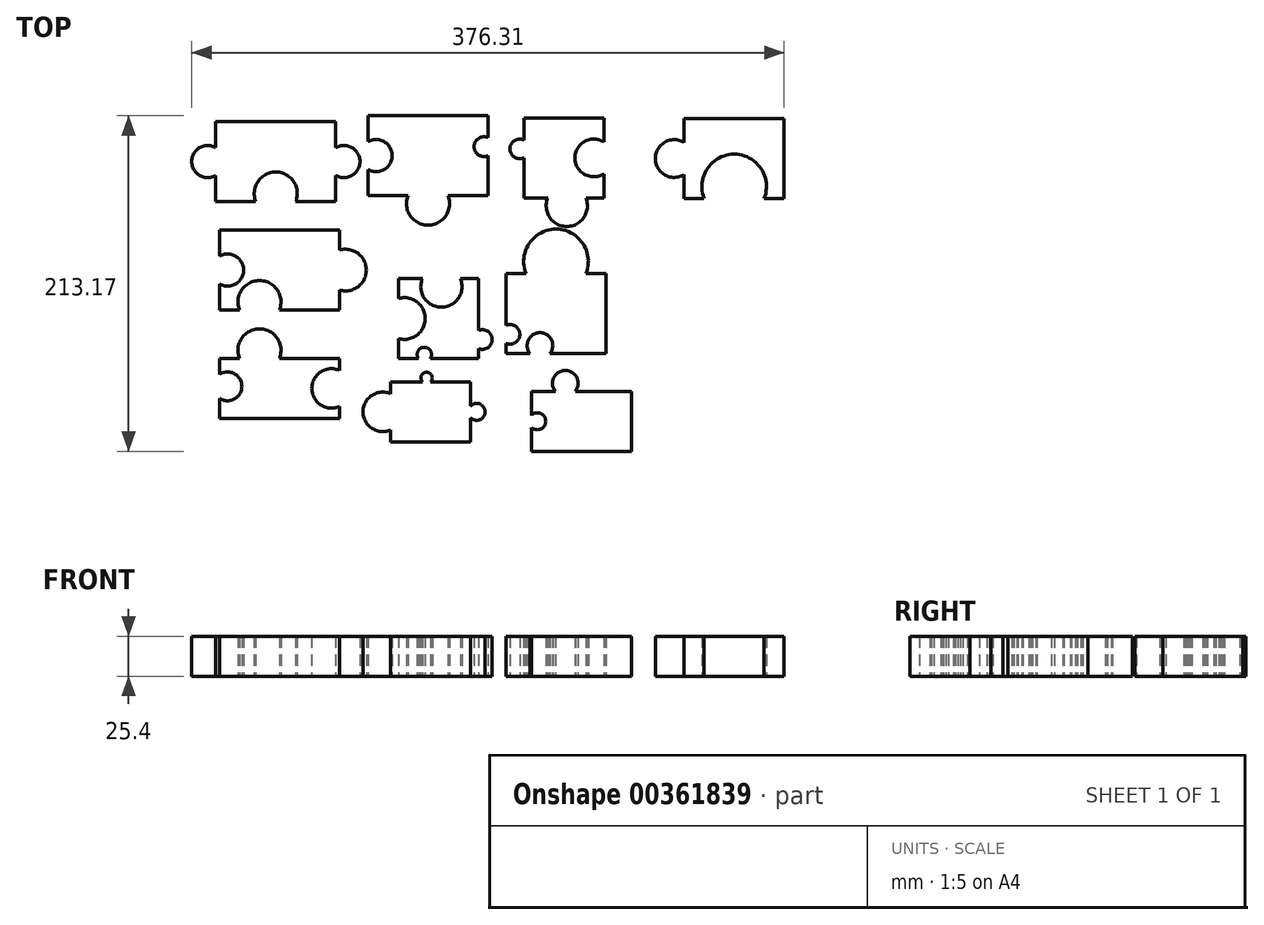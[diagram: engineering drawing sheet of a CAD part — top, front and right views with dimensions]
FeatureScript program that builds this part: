
annotation { "Feature Type Name" : "Feature", "Feature Type Description" : "" }
export const myFeature = defineFeature(function(context is Context, id is Id, definition is map)
    precondition{}
    {
        {
            var Q0;
            Q0=qCreatedBy(makeId("Top.planeOp"),FACE);
            var sketch = newSketch(context, id + "F0", { "sketchPlane" : qUnion([Q0])});
            skLineSegment(sketch, "E0.bottom", {"start": v(-78.54, 63.45) * mm, "end": v(-2.34, 63.45) * mm});
            skLineSegment(sketch, "E0.top", {"start": v(-78.54, 12.65) * mm, "end": v(-2.34, 12.65) * mm});
            skLineSegment(sketch, "E0.left", {"start": v(-78.54, 63.45) * mm, "end": v(-78.54, 12.65) * mm});
            skLineSegment(sketch, "E0.right", {"start": v(-2.34, 63.45) * mm, "end": v(-2.34, 12.65) * mm});
            skArc(sketch, "E1", {"start": v(-27.74, 12.65) * mm, "mid": v(-40.44, 31.4) * mm, "end": v(-53.14, 12.65) * mm});
            skArc(sketch, "E2", {"start": v(-78.54, 46.94) * mm, "mid": v(-93.86, 38.05) * mm, "end": v(-78.54, 29.16) * mm});
            skArc(sketch, "E3", {"start": v(-2.34, 29.16) * mm, "mid": v(12.98, 38.05) * mm, "end": v(-2.34, 46.94) * mm});
            skSolve(sketch);
        }
        {
            var Q0;
            {var subQ0=sQuery(id+"F0.wireOp",EDGE,"E2");Q0=makeQuery(id+"F0.imprint","IMPRINT",FACE,{"disambiguationData":[TD([[makeQuery(id+"F0.imprint","IMPRINT",EDGE,{"derivedFrom":subQ0}),1.0]])]});}
            var Q1;
            {var subQ1=sQuery(id+"F0.wireOp",EDGE,"E0.bottom");Q1=makeQuery(id+"F0.imprint","IMPRINT",FACE,{"disambiguationData":[TD([[makeQuery(id+"F0.imprint","IMPRINT",EDGE,{"derivedFrom":subQ1}),-1.0]])]});}
            var Q2;
            {var subQ0=sQuery(id+"F0.wireOp",EDGE,"E3");Q2=makeQuery(id+"F0.imprint","IMPRINT",FACE,{"disambiguationData":[TD([[makeQuery(id+"F0.imprint","IMPRINT",EDGE,{"derivedFrom":subQ0}),1.0]])]});}
            extrude(context, id + "F1", {"entities" : qUnion([Q0, Q1, Q2]), "depth" : 25.4 * mm});
        }
        {
            var Q0;
            Q0=qCreatedBy(makeId("Top.planeOp"),FACE);
            var sketch = newSketch(context, id + "F2", { "sketchPlane" : qUnion([Q0])});
            skLineSegment(sketch, "E4.bottom", {"start": v(18.15, 67.2) * mm, "end": v(94.35, 67.2) * mm});
            skLineSegment(sketch, "E4.top", {"start": v(18.15, 16.4) * mm, "end": v(94.35, 16.4) * mm});
            skLineSegment(sketch, "E4.left", {"start": v(18.15, 67.2) * mm, "end": v(18.15, 16.4) * mm});
            skLineSegment(sketch, "E4.right", {"start": v(94.35, 67.2) * mm, "end": v(94.35, 16.4) * mm});
            skArc(sketch, "E5", {"start": v(18.15, 32.91) * mm, "mid": v(33.47, 41.8) * mm, "end": v(18.15, 50.7) * mm});
            skArc(sketch, "E6", {"start": v(43.55, 16.4) * mm, "mid": v(56.25, -2.35) * mm, "end": v(68.95, 16.4) * mm});
            skArc(sketch, "E7", {"start": v(94.35, 53.23) * mm, "mid": v(85.55, 47.52) * mm, "end": v(94.35, 41.8) * mm});
            skSolve(sketch);
        }
        {
            var Q0;
            {var subQ0=sQuery(id+"F2.wireOp",EDGE,"E6");Q0=makeQuery(id+"F2.imprint","IMPRINT",FACE,{"disambiguationData":[TD([[makeQuery(id+"F2.imprint","IMPRINT",EDGE,{"derivedFrom":subQ0}),1.0]])]});}
            var Q1;
            {var subQ7=sQuery(id+"F2.wireOp",EDGE,"E4.bottom");Q1=makeQuery(id+"F2.imprint","IMPRINT",FACE,{"disambiguationData":[TD([[makeQuery(id+"F2.imprint","IMPRINT",EDGE,{"derivedFrom":subQ7}),-1.0]])]});}
            var Q2;
            Q2 = qSketchRegion(id + "F8", true);
            extrude(context, id + "F3", {"entities" : qUnion([Q0, Q1, Q2]), "depth" : 25.4 * mm});
        }
        {
            var Q0;
            Q0=qCreatedBy(makeId("Top.planeOp"),FACE);
            var sketch = newSketch(context, id + "F4", { "sketchPlane" : qUnion([Q0])});
            skLineSegment(sketch, "E8.bottom", {"start": v(-76.2, -5.49) * mm, "end": v(0, -5.49) * mm});
            skLineSegment(sketch, "E8.top", {"start": v(-76.2, -56.29) * mm, "end": v(0, -56.29) * mm});
            skLineSegment(sketch, "E8.left", {"start": v(-76.2, -5.49) * mm, "end": v(-76.2, -56.29) * mm});
            skLineSegment(sketch, "E8.right", {"start": v(0, -5.49) * mm, "end": v(0, -56.29) * mm});
            skArc(sketch, "E9", {"start": v(-76.2, -39.78) * mm, "mid": v(-60.88, -30.89) * mm, "end": v(-76.2, -22) * mm});
            skArc(sketch, "E10", {"start": v(-50.8, -5.49) * mm, "mid": v(-38.1, -24.24) * mm, "end": v(-25.4, -5.49) * mm});
            skArc(sketch, "E11", {"start": v(0, -43.59) * mm, "mid": v(17.07, -30.89) * mm, "end": v(0, -18.19) * mm});
            skArc(sketch, "E12", {"start": v(-38.1, -56.29) * mm, "mid": v(-50.8, -37.53) * mm, "end": v(-63.5, -56.29) * mm});
            skSolve(sketch);
        }
        {
            var Q0;
            {var subQ3=sQuery(id+"F4.wireOp",EDGE,"E8.bottom");Q0=makeQuery(id+"F4.imprint","IMPRINT",FACE,{"disambiguationData":[TD([[makeQuery(id+"F4.imprint","IMPRINT",EDGE,{"derivedFrom":subQ3}),-1.0]])]});}
            var Q1;
            Q1 = qSketchRegion(id + "F6", true);
            var Q2;
            {var subQ0=sQuery(id+"F4.wireOp",EDGE,"E11");Q2=makeQuery(id+"F4.imprint","IMPRINT",FACE,{"disambiguationData":[TD([[makeQuery(id+"F4.imprint","IMPRINT",EDGE,{"derivedFrom":subQ0}),1.0]])]});}
            var Q3;
            {var subQ0=sQuery(id+"F4.wireOp",EDGE,"E9");Q3=makeQuery(id+"F4.imprint","IMPRINT",FACE,{"disambiguationData":[TD([[makeQuery(id+"F4.imprint","IMPRINT",EDGE,{"derivedFrom":subQ0}),-1.0]])]});}
            extrude(context, id + "F5", {"entities" : qUnion([Q0, Q1, Q2, Q3]), "depth" : 25.4 * mm});
        }
        {
            var Q0;
            Q0=qCreatedBy(makeId("Top.planeOp"),FACE);
            var sketch = newSketch(context, id + "F6", { "sketchPlane" : qUnion([Q0])});
            skLineSegment(sketch, "E13.bottom", {"start": v(37.43, -36.24) * mm, "end": v(88.23, -36.24) * mm});
            skLineSegment(sketch, "E13.top", {"start": v(37.43, -87.04) * mm, "end": v(88.23, -87.04) * mm});
            skLineSegment(sketch, "E13.left", {"start": v(37.43, -36.24) * mm, "end": v(37.43, -87.04) * mm});
            skLineSegment(sketch, "E13.right", {"start": v(88.23, -36.24) * mm, "end": v(88.23, -87.04) * mm});
            skArc(sketch, "E14", {"start": v(37.43, -74.34) * mm, "mid": v(54.5, -61.64) * mm, "end": v(37.43, -48.94) * mm});
            skArc(sketch, "E15", {"start": v(52.67, -36.24) * mm, "mid": v(64.73, -54.42) * mm, "end": v(76.8, -36.24) * mm});
            skArc(sketch, "E16", {"start": v(88.23, -80.7) * mm, "mid": v(97.02, -74.98) * mm, "end": v(88.23, -69.26) * mm});
            skArc(sketch, "E17", {"start": v(50.13, -87.04) * mm, "mid": v(53.94, -79.93) * mm, "end": v(57.75, -87.04) * mm});
            skSolve(sketch);
        }
        {
            var Q0;
            {var subQ0=sQuery(id+"F6.wireOp",EDGE,"E16");Q0=makeQuery(id+"F6.imprint","IMPRINT",FACE,{"disambiguationData":[TD([[makeQuery(id+"F6.imprint","IMPRINT",EDGE,{"derivedFrom":subQ0}),1.0]])]});}
            var Q1;
            {var subQ0=sQuery(id+"F6.wireOp",EDGE,"E14");Q1=makeQuery(id+"F6.imprint","IMPRINT",FACE,{"disambiguationData":[TD([[makeQuery(id+"F6.imprint","IMPRINT",EDGE,{"derivedFrom":subQ0}),-1.0]])]});}
            extrude(context, id + "F7", {"entities" : qUnion([Q0, Q1]), "depth" : 25.4 * mm});
        }
        {
            var Q0;
            Q0=qCreatedBy(makeId("Top.planeOp"),FACE);
            var sketch = newSketch(context, id + "F8", { "sketchPlane" : qUnion([Q0])});
            skLineSegment(sketch, "E18.bottom", {"start": v(117.1, 14.97) * mm, "end": v(167.9, 14.97) * mm});
            skLineSegment(sketch, "E18.top", {"start": v(117.1, 65.77) * mm, "end": v(167.9, 65.77) * mm});
            skLineSegment(sketch, "E18.left", {"start": v(117.1, 14.97) * mm, "end": v(117.1, 65.77) * mm});
            skLineSegment(sketch, "E18.right", {"start": v(167.9, 14.97) * mm, "end": v(167.9, 65.77) * mm});
            skArc(sketch, "E19", {"start": v(132.33, 14.97) * mm, "mid": v(144.4, -3.2) * mm, "end": v(156.46, 14.97) * mm});
            skArc(sketch, "E20", {"start": v(117.1, 51.8) * mm, "mid": v(108.3, 46.09) * mm, "end": v(117.1, 40.37) * mm});
            skArc(sketch, "E21", {"start": v(167.9, 50.53) * mm, "mid": v(149.56, 40.37) * mm, "end": v(167.9, 30.21) * mm});
            skSolve(sketch);
        }
        {
            var Q0;
            {var subQ0=sQuery(id+"F8.wireOp",EDGE,"LlIyA9nJ-b66G-0byr-U1jV-6pKlKF7MGgKk");Q0=makeQuery(id+"F8.imprint","IMPRINT",FACE,{"disambiguationData":[TD([[makeQuery(id+"F8.imprint","IMPRINT",EDGE,{"derivedFrom":subQ0}),1.0]])]});}
            var Q1;
            {var subQ0=sQuery(id+"F8.wireOp",EDGE,"E18.top");Q1=makeQuery(id+"F8.imprint","IMPRINT",FACE,{"disambiguationData":[TD([[makeQuery(id+"F8.imprint","IMPRINT",EDGE,{"derivedFrom":subQ0}),-1.0]])]});}
            var Q2;
            {var subQ0=sQuery(id+"F8.wireOp",EDGE,"E19");Q2=makeQuery(id+"F8.imprint","IMPRINT",FACE,{"disambiguationData":[TD([[makeQuery(id+"F8.imprint","IMPRINT",EDGE,{"derivedFrom":subQ0}),1.0]])]});}
            var Q3;
            {var subQ0=sQuery(id+"F8.wireOp",EDGE,"E20");Q3=makeQuery(id+"F8.imprint","IMPRINT",FACE,{"disambiguationData":[TD([[makeQuery(id+"F8.imprint","IMPRINT",EDGE,{"derivedFrom":subQ0}),1.0]])]});}
            extrude(context, id + "F9", {"entities" : qUnion([Q0, Q1, Q2, Q3]), "depth" : 25.4 * mm});
        }
        {
            var Q0;
            Q0=qCreatedBy(makeId("Top.planeOp"),FACE);
            var sketch = newSketch(context, id + "F10", { "sketchPlane" : qUnion([Q0])});
            skLineSegment(sketch, "E22.bottom", {"start": v(218.95, 65.36) * mm, "end": v(282.45, 65.36) * mm});
            skLineSegment(sketch, "E22.top", {"start": v(218.95, 14.56) * mm, "end": v(282.45, 14.56) * mm});
            skLineSegment(sketch, "E22.left", {"start": v(218.95, 65.36) * mm, "end": v(218.95, 14.56) * mm});
            skLineSegment(sketch, "E22.right", {"start": v(282.45, 65.36) * mm, "end": v(282.45, 14.56) * mm});
            skArc(sketch, "E23", {"start": v(218.95, 50.12) * mm, "mid": v(200.62, 39.96) * mm, "end": v(218.95, 29.8) * mm});
            skArc(sketch, "E24", {"start": v(269.75, 14.56) * mm, "mid": v(250.7, 42.7) * mm, "end": v(231.65, 14.56) * mm});
            skSolve(sketch);
        }
        {
            var Q0;
            {var subQ0=sQuery(id+"F10.wireOp",EDGE,"E23");Q0=makeQuery(id+"F10.imprint","IMPRINT",FACE,{"disambiguationData":[TD([[makeQuery(id+"F10.imprint","IMPRINT",EDGE,{"derivedFrom":subQ0}),1.0]])]});}
            var Q1;
            {var subQ1=sQuery(id+"F10.wireOp",EDGE,"E22.bottom");Q1=makeQuery(id+"F10.imprint","IMPRINT",FACE,{"disambiguationData":[TD([[makeQuery(id+"F10.imprint","IMPRINT",EDGE,{"derivedFrom":subQ1}),-1.0]])]});}
            extrude(context, id + "F11", {"entities" : qUnion([Q0, Q1]), "depth" : 25.4 * mm});
        }
        {
            var Q0;
            Q0=qCreatedBy(makeId("Top.planeOp"),FACE);
            var sketch = newSketch(context, id + "F12", { "sketchPlane" : qUnion([Q0])});
            skLineSegment(sketch, "E25.bottom", {"start": v(105.77, -33.02) * mm, "end": v(169.27, -33.02) * mm});
            skLineSegment(sketch, "E25.top", {"start": v(105.77, -83.82) * mm, "end": v(169.27, -83.82) * mm});
            skLineSegment(sketch, "E25.left", {"start": v(105.77, -33.02) * mm, "end": v(105.77, -83.82) * mm});
            skLineSegment(sketch, "E25.right", {"start": v(169.27, -33.02) * mm, "end": v(169.27, -83.82) * mm});
            skArc(sketch, "E26", {"start": v(105.77, -77.47) * mm, "mid": v(114.56, -71.76) * mm, "end": v(105.77, -66.04) * mm});
            skArc(sketch, "E27", {"start": v(156.57, -33.02) * mm, "mid": v(137.52, -4.88) * mm, "end": v(118.47, -33.02) * mm});
            skArc(sketch, "E28", {"start": v(133.7, -83.82) * mm, "mid": v(127.36, -70.6) * mm, "end": v(121, -83.82) * mm});
            skSolve(sketch);
        }
        {
            var Q0;
            {var subQ0=sQuery(id+"F12.wireOp",EDGE,"E27");Q0=makeQuery(id+"F12.imprint","IMPRINT",FACE,{"disambiguationData":[TD([[makeQuery(id+"F12.imprint","IMPRINT",EDGE,{"derivedFrom":subQ0}),1.0]])]});}
            var Q1;
            {var subQ0=sQuery(id+"F12.wireOp",EDGE,"E25.top");Q1=makeQuery(id+"F12.imprint","IMPRINT",FACE,{"disambiguationData":[TD([[makeQuery(id+"F12.imprint","IMPRINT",EDGE,{"derivedFrom":subQ0}),1.0]])]});}
            extrude(context, id + "F13", {"entities" : qUnion([Q0, Q1]), "depth" : 25.4 * mm});
        }
        {
            var Q0;
            Q0=qCreatedBy(makeId("Top.planeOp"),FACE);
            var sketch = newSketch(context, id + "F14", { "sketchPlane" : qUnion([Q0])});
            skLineSegment(sketch, "E29.bottom", {"start": v(-76.2, -86.97) * mm, "end": v(0, -86.97) * mm});
            skLineSegment(sketch, "E29.top", {"start": v(-76.2, -125.07) * mm, "end": v(0, -125.07) * mm});
            skLineSegment(sketch, "E29.left", {"start": v(-76.2, -86.97) * mm, "end": v(-76.2, -125.07) * mm});
            skLineSegment(sketch, "E29.right", {"start": v(0, -86.97) * mm, "end": v(0, -125.07) * mm});
            skArc(sketch, "E30", {"start": v(-76.2, -112.37) * mm, "mid": v(-61.96, -104.75) * mm, "end": v(-76.2, -97.13) * mm});
            skArc(sketch, "E31", {"start": v(-38.1, -86.97) * mm, "mid": v(-50.8, -68.21) * mm, "end": v(-63.5, -86.97) * mm});
            skArc(sketch, "E32", {"start": v(0, -94.6) * mm, "mid": v(-17.59, -106.02) * mm, "end": v(0, -117.45) * mm});
            skSolve(sketch);
        }
        {
            var Q0;
            {var subQ0=sQuery(id+"F14.wireOp",EDGE,"E31");Q0=makeQuery(id+"F14.imprint","IMPRINT",FACE,{"disambiguationData":[TD([[makeQuery(id+"F14.imprint","IMPRINT",EDGE,{"derivedFrom":subQ0}),1.0]])]});}
            var Q1;
            {var subQ0=sQuery(id+"F14.wireOp",EDGE,"E29.top");Q1=makeQuery(id+"F14.imprint","IMPRINT",FACE,{"disambiguationData":[TD([[makeQuery(id+"F14.imprint","IMPRINT",EDGE,{"derivedFrom":subQ0}),1.0]])]});}
            extrude(context, id + "F15", {"entities" : qUnion([Q0, Q1]), "depth" : 25.4 * mm});
        }
        {
            var Q0;
            Q0=qCreatedBy(makeId("Top.planeOp"),FACE);
            var sketch = newSketch(context, id + "F16", { "sketchPlane" : qUnion([Q0])});
            skLineSegment(sketch, "E33.bottom", {"start": v(32.52, -101.88) * mm, "end": v(83.32, -101.88) * mm});
            skLineSegment(sketch, "E33.top", {"start": v(32.52, -139.98) * mm, "end": v(83.32, -139.98) * mm});
            skLineSegment(sketch, "E33.left", {"start": v(32.52, -101.88) * mm, "end": v(32.52, -139.98) * mm});
            skLineSegment(sketch, "E33.right", {"start": v(83.32, -101.88) * mm, "end": v(83.32, -139.98) * mm});
            skArc(sketch, "E34", {"start": v(32.52, -109.5) * mm, "mid": v(14.93, -120.93) * mm, "end": v(32.52, -132.36) * mm});
            skArc(sketch, "E35", {"start": v(57.92, -101.88) * mm, "mid": v(55.38, -95.74) * mm, "end": v(52.84, -101.88) * mm});
            skArc(sketch, "E36", {"start": v(83.32, -124.74) * mm, "mid": v(92.52, -120.93) * mm, "end": v(83.32, -117.12) * mm});
            skSolve(sketch);
        }
        {
            var Q0;
            Q0 = qSketchRegion(id + "F16", true);
            extrude(context, id + "F17", {"entities" : qUnion([Q0]), "depth" : 25.4 * mm});
        }
        {
            var Q0;
            Q0=qCreatedBy(makeId("Top.planeOp"),FACE);
            var sketch = newSketch(context, id + "F18", { "sketchPlane" : qUnion([Q0])});
            skLineSegment(sketch, "E37.bottom", {"start": v(121.84, -107.87) * mm, "end": v(185.34, -107.87) * mm});
            skLineSegment(sketch, "E37.top", {"start": v(121.84, -145.97) * mm, "end": v(185.34, -145.97) * mm});
            skLineSegment(sketch, "E37.left", {"start": v(121.84, -107.87) * mm, "end": v(121.84, -145.97) * mm});
            skLineSegment(sketch, "E37.right", {"start": v(185.34, -107.87) * mm, "end": v(185.34, -145.97) * mm});
            skArc(sketch, "E38", {"start": v(121.84, -130.73) * mm, "mid": v(131.04, -126.92) * mm, "end": v(121.84, -123.11) * mm});
            skArc(sketch, "E39", {"start": v(149.78, -107.87) * mm, "mid": v(143.43, -94.66) * mm, "end": v(137.08, -107.87) * mm});
            skSolve(sketch);
        }
        {
            var Q0;
            {var subQ0=sQuery(id+"F18.wireOp",EDGE,"E39");Q0=makeQuery(id+"F18.imprint","IMPRINT",FACE,{"disambiguationData":[TD([[makeQuery(id+"F18.imprint","IMPRINT",EDGE,{"derivedFrom":subQ0}),1.0]])]});}
            var Q1;
            {var subQ0=sQuery(id+"F18.wireOp",EDGE,"E37.top");Q1=makeQuery(id+"F18.imprint","IMPRINT",FACE,{"disambiguationData":[TD([[makeQuery(id+"F18.imprint","IMPRINT",EDGE,{"derivedFrom":subQ0}),1.0]])]});}
            extrude(context, id + "F19", {"entities" : qUnion([Q0, Q1]), "depth" : 25.4 * mm});
        }
    });
